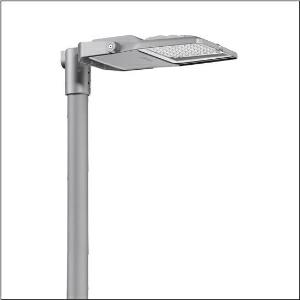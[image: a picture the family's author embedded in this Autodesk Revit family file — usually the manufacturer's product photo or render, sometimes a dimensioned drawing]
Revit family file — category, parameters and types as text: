
# Revit family: floodlight_fl_21_iq_mini___pl52_5xa7771b4d3a_0091
name_source: partatom
category: Lighting Fixtures
units: mm (PartAtom-declared; Revit-internal decimal feet)

## family parameters
Cut with Voids When Loaded = No
Host = Face
Light Source = No
Part Type = Normal
Room Calculation Point = No
Round Connector Dimension = Use Diameter
Shared = No

## types (1)
- --- (1 x LED, 6490 lm, 45.5 W, 4000K)
    Apparent Load = 46 VA
    CIE Flux Codes = 26 60 98 100 100
    Color Rendering = 70
    Color Temperature = 4000K
    Default Elevation = 1800 mm
    Description = Floodlight FL 21 iQ mini, floodlight, primary light control with lens, of PMMA, primary optical cover: protective disc, of toughened safety glass, transparent, light distribution: PL52, light emission: direct distribution, installation type: surface-mounted, LED, High Power LED, rated luminous flux: 6.490lm, luminous efficacy: 143lm/W, light colour: 740, colour temperature: 4000K, control: Auto-Match, Temp-Guard, Lumen-Switch, Night-Set, Smart-Wire, Light-Fading, Desk-Remote (wireless, voltage-free reading and setting of iQ features in the workshop via application-optimized NFC function/RFID function), optimised constant luminous flux control (CLO 2.0), with terminal, 6-pole, mains connection: 220..240V, AC, 50/60Hz, start of lifetime: 46W, end of service life: 48W, reduction: 22W, luminaire housing, of diecast aluminium, powder-coated, Siteco® metallic grey (DB 702S), corrosivity category C5 mid according to DIN EN ISO 12944, sealing non-destructively replaceable, please order mast flange separately, mast bracket, of steel, galvanised, powder-coated, Siteco® metallic grey (DB 702S), protection rating (complete): IP66, insulation class (complete): insulation class II (safety insulation), certification: CE, ENEC, VDE, protection symbol: D, impact resistance: IK08, permissible operating ambient temperature: -40..+40°C, permissible operating ambient temperature for outdoor applications: -40..+50°C, standard: DIN EN 12944, LABS conformity tested according to VDMA 24364:2018-05, packaging unit: 1 piece

Light Distribution: PL52
    Height = 70 mm
    Lamp = 1 x LED
    Lamp Light Flux = 6490 lm
    Lamp Power = 45.5 W
    Lamp count = 1
    Length = 485 mm
    Luminous efficacy = 143 lm/W
    Manufacturer = Siteco
    ModVariant = No
    Model = 5XA7771B4D3A
    Number of Poles = 1
    OnlyDefault = Yes
    Power Factor = 1
    Product Name = Floodlight FL 21 iQ mini | PL52
    Product group = floodlight | pylon annexe
    ProductGroupID = 6200
    Protection Class = Protection class II
    Protection Degree = IP 66
    RLX_Detail_Level = 1
    RLX_Emergency_Light_Flux = 0 lm
    RLX_Emergency_Type = 0
    RLX_Emergency_Type_DB = No
    RlxData = <blob elided: 101373 chars, md5=2654f724>
    Socket = socket
    Standby Power = 0 W
    System Light Flux = 6490 lm
    System Power = 46 W
    Type Comments = factory setting: luminous flux: 100 % | dim-lin: 254 | 463 mA
    Type Image = l_1007125.jpg
    URL = http://relux.com
    VarID = @adj_115139
    Voltage = 0 V
    Weight = 0.00 kg
    Width = 337 mm

## geometry (parser evidence)
native form markers: Blend x4, Sweep x11
no freeform markers — native parametric forms only
